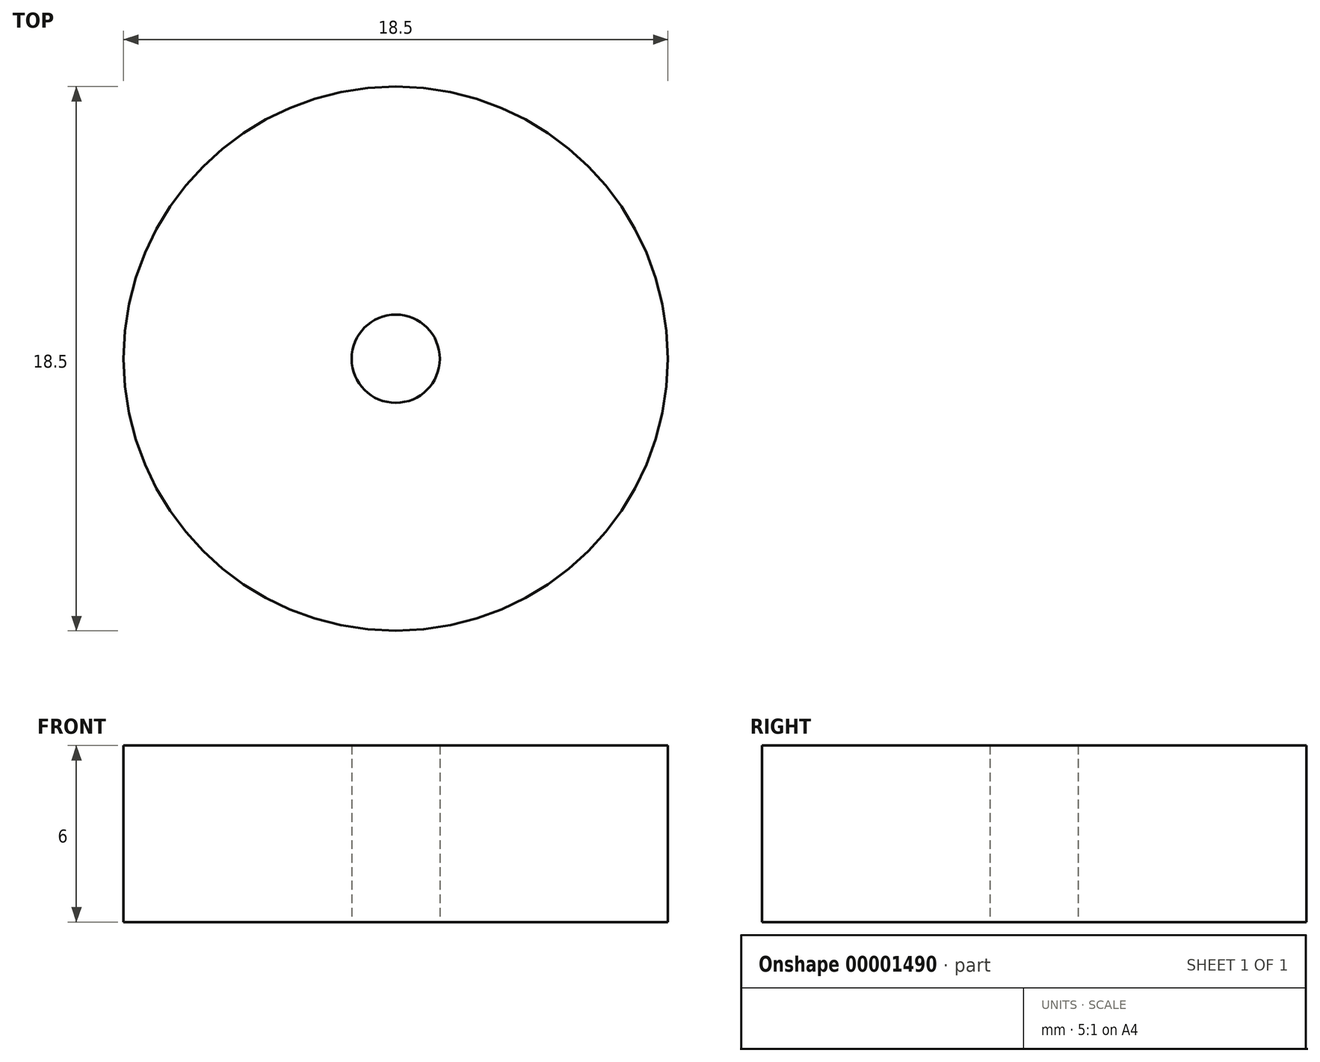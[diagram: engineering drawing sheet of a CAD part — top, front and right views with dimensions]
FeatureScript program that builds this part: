
annotation { "Feature Type Name" : "Feature", "Feature Type Description" : "" }
export const myFeature = defineFeature(function(context is Context, id is Id, definition is map)
    precondition{}
    {
        {
            var Q0;
            Q0=qCreatedBy(makeId("Top.planeOp"),FACE);
            var sketch = newSketch(context, id + "F0", { "sketchPlane" : qUnion([Q0])});
            skCircle(sketch, "E0", {"center": v(0, 0) * mm, "radius": 9.25 * mm});
            skCircle(sketch, "E1", {"center": v(0, 0) * mm, "radius": 1.5 * mm});
            skSolve(sketch);
        }
        {
            var Q0;
            Q0=makeQuery(id+"F0.imprint","IMPRINT",FACE,{"disambiguationData":[TD([[makeQuery(id+"F0.imprint","IMPRINT",EDGE,{"derivedFrom":sQuery(id+"F0.wireOp",EDGE,"E0")}),1.0]])]});
            extrude(context, id + "F1", {"entities" : qUnion([Q0]), "depth" : 6 * mm});
        }
    });
